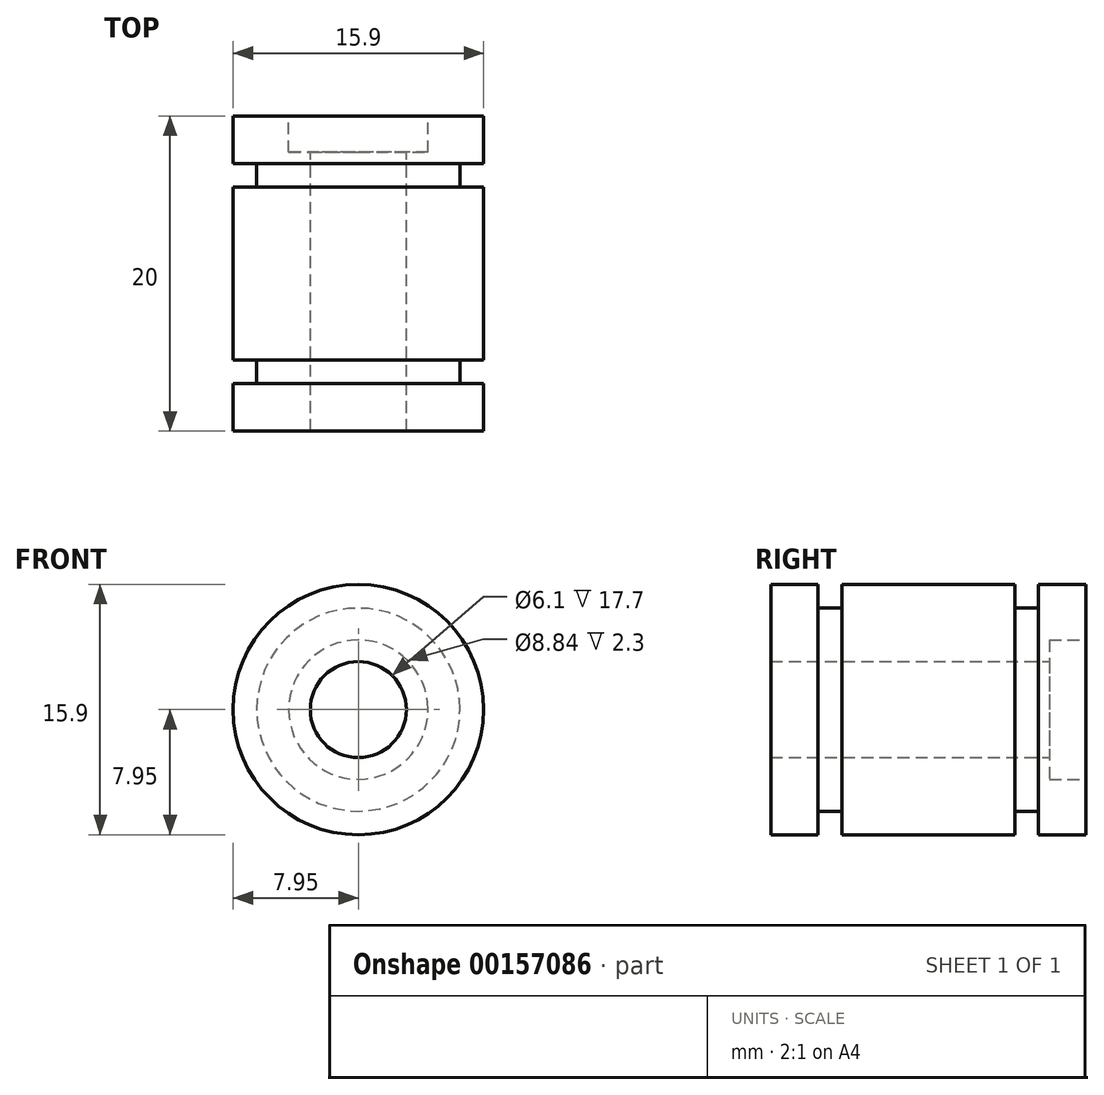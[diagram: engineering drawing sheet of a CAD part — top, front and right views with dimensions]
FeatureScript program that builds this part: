
annotation { "Feature Type Name" : "Feature", "Feature Type Description" : "" }
export const myFeature = defineFeature(function(context is Context, id is Id, definition is map)
    precondition{}
    {
        {
            var Q0;
            Q0=qCreatedBy(makeId("Right.planeOp"),FACE);
            var sketch = newSketch(context, id + "F0", { "sketchPlane" : qUnion([Q0])});
            skLineSegment(sketch, "E0", {"start": v(11.47, 0) * mm, "end": v(0, 0) * mm, "construction": true});
            skLineSegment(sketch, "E1", {"start": v(17.7, 3.05) * mm, "end": v(0, 3.05) * mm});
            skLineSegment(sketch, "E2", {"start": v(17.7, 3.05) * mm, "end": v(17.7, 4.42) * mm});
            skLineSegment(sketch, "E3", {"start": v(20, 4.42) * mm, "end": v(17.7, 4.42) * mm});
            skLineSegment(sketch, "E4", {"start": v(20, 4.42) * mm, "end": v(20, 7.95) * mm});
            skLineSegment(sketch, "E5", {"start": v(17, 7.95) * mm, "end": v(20, 7.95) * mm});
            skLineSegment(sketch, "E6", {"start": v(17, 7.95) * mm, "end": v(17, 6.45) * mm});
            skLineSegment(sketch, "E7", {"start": v(15.5, 6.45) * mm, "end": v(17, 6.45) * mm});
            skLineSegment(sketch, "E8", {"start": v(3, 6.45) * mm, "end": v(3, 7.95) * mm});
            skLineSegment(sketch, "E9", {"start": v(0, 7.95) * mm, "end": v(3, 7.95) * mm});
            skLineSegment(sketch, "E10", {"start": v(0, 7.95) * mm, "end": v(0, 3.05) * mm});
            skLineSegment(sketch, "E11", {"start": v(4.5, 6.45) * mm, "end": v(4.5, 7.95) * mm});
            skLineSegment(sketch, "E12", {"start": v(4.5, 7.95) * mm, "end": v(15.5, 7.95) * mm});
            skLineSegment(sketch, "E13", {"start": v(15.5, 7.95) * mm, "end": v(15.5, 6.45) * mm});
            skLineSegment(sketch, "E14.trimOffspring", {"start": v(4.5, 6.45) * mm, "end": v(3, 6.45) * mm});
            skSolve(sketch);
        }
        {
            var Q0;
            Q0=makeQuery(id+"F0.imprint","IMPRINT",FACE,{"disambiguationData":[TD([[makeQuery(id+"F0.imprint","IMPRINT",EDGE,{"derivedFrom":sQuery(id+"F0.wireOp",EDGE,"E1")}),-1.0]])]});
            var Q1;
            Q1=sQuery(id+"F0.wireOp",EDGE,"E0");
            revolve(context, id + "F1", {"entities" : qUnion([Q0]), "axis" : qUnion([Q1]), "revolveType" : RevolveType.FULL});
        }
    });
